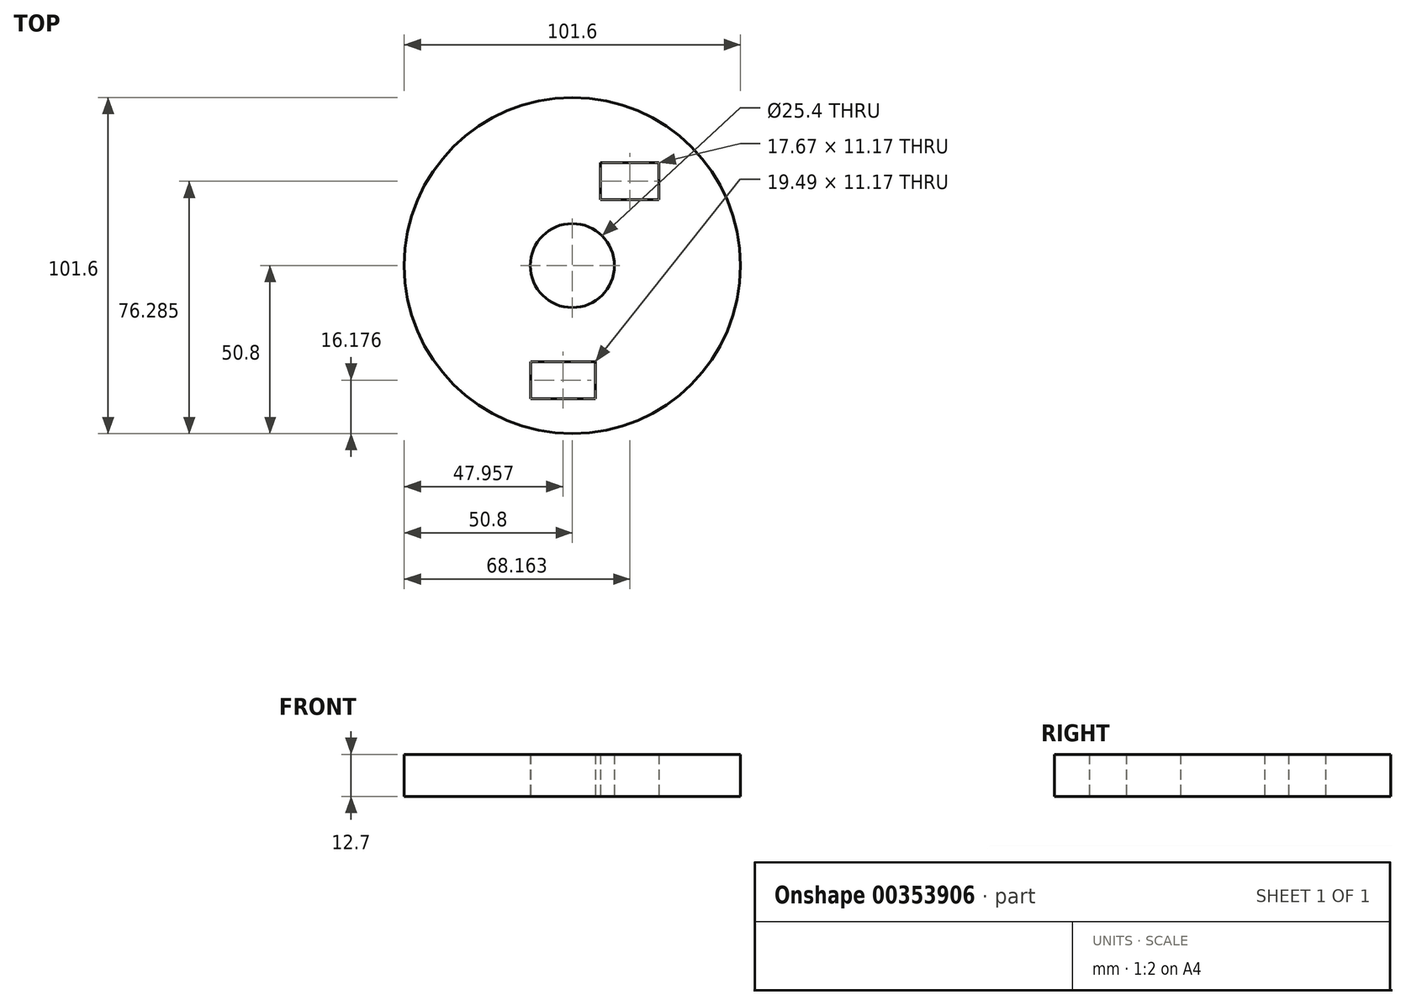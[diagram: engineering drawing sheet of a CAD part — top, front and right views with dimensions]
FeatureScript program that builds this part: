
annotation { "Feature Type Name" : "Feature", "Feature Type Description" : "" }
export const myFeature = defineFeature(function(context is Context, id is Id, definition is map)
    precondition{}
    {
        {
            var Q0;
            Q0=qCreatedBy(makeId("Top.planeOp"),FACE);
            var sketch = newSketch(context, id + "F0", { "sketchPlane" : qUnion([Q0])});
            skCircle(sketch, "E0", {"center": v(0, 0) * mm, "radius": 50.8 * mm});
            skCircle(sketch, "E1", {"center": v(0, 0) * mm, "radius": 12.7 * mm});
            skLineSegment(sketch, "E2.bottom", {"start": v(8.53, 31.07) * mm, "end": v(26.2, 31.07) * mm});
            skLineSegment(sketch, "E2.top", {"start": v(8.53, 19.9) * mm, "end": v(26.2, 19.9) * mm});
            skLineSegment(sketch, "E2.left", {"start": v(8.53, 31.07) * mm, "end": v(8.53, 19.9) * mm});
            skLineSegment(sketch, "E2.right", {"start": v(26.2, 31.07) * mm, "end": v(26.2, 19.9) * mm});
            skLineSegment(sketch, "E3.bottom", {"start": v(-12.6, -29.04) * mm, "end": v(6.9, -29.04) * mm});
            skLineSegment(sketch, "E3.top", {"start": v(-12.6, -40.2) * mm, "end": v(6.9, -40.2) * mm});
            skLineSegment(sketch, "E3.left", {"start": v(-12.6, -29.04) * mm, "end": v(-12.6, -40.2) * mm});
            skLineSegment(sketch, "E3.right", {"start": v(6.9, -29.04) * mm, "end": v(6.9, -40.2) * mm});
            skSolve(sketch);
        }
        {
            var Q0;
            Q0=makeQuery(id+"F0.imprint","IMPRINT",FACE,{"disambiguationData":[TD([[makeQuery(id+"F0.imprint","IMPRINT",EDGE,{"derivedFrom":sQuery(id+"F0.wireOp",EDGE,"E0")}),1.0]])]});
            extrude(context, id + "F1", {"entities" : qUnion([Q0]), "endBound" : BoundingType.SYMMETRIC, "depth" : 12.7 * mm});
        }
    });
